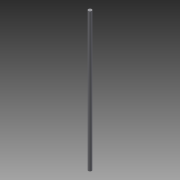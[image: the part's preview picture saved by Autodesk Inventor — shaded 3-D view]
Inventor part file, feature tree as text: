
AUTODESK INVENTOR PART (.ipt)
format: ipt  version: 2013 (Build 170138000, 138)  size: 61,440 bytes
history: native  units: in
note: dims shown in document units (in); Inventor stores cm internally (conversion verified against a paired STEP export)
features: extrude x1, sketch x1
ambient origin geometry x8: Origin, YZ Plane, XZ Plane, XY Plane, X Axis, Y Axis, Z Axis, Center Point
bodies: Solid1 (feature_tree)
feature tree (2):
  extrude  "Extrusion1"  Depth=20.25in TaperAngle=0.0deg
  sketch  "Sketch1"  dims[d0=0.5in d1=20.25in d2=0.0in]
